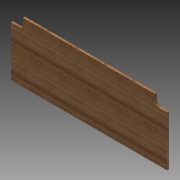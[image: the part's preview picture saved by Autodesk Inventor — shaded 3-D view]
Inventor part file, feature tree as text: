
AUTODESK INVENTOR PART (.ipt)
format: ipt  version: 2012 (Build 160160000, 160)  size: 100,864 bytes
history: native  units: in
note: dims shown in document units (in); Inventor stores cm internally (conversion verified against a paired STEP export)
features: extrude x1, sketch x1
ambient origin geometry x8: Origin, YZ Plane, XZ Plane, XY Plane, X Axis, Y Axis, Z Axis, Center Point
bodies: Solid1 (feature_tree)
feature tree (2):
  extrude  "Extrusion1"  Depth=19.5in
  sketch  "Sketch1"  dims[d0=7.5in d1=19.5in d2=0.25in d3=0.0in d4=1.0in d5=1.0in d6=1.0in d7=0.75in d8=1.0in d9=0.75in]
